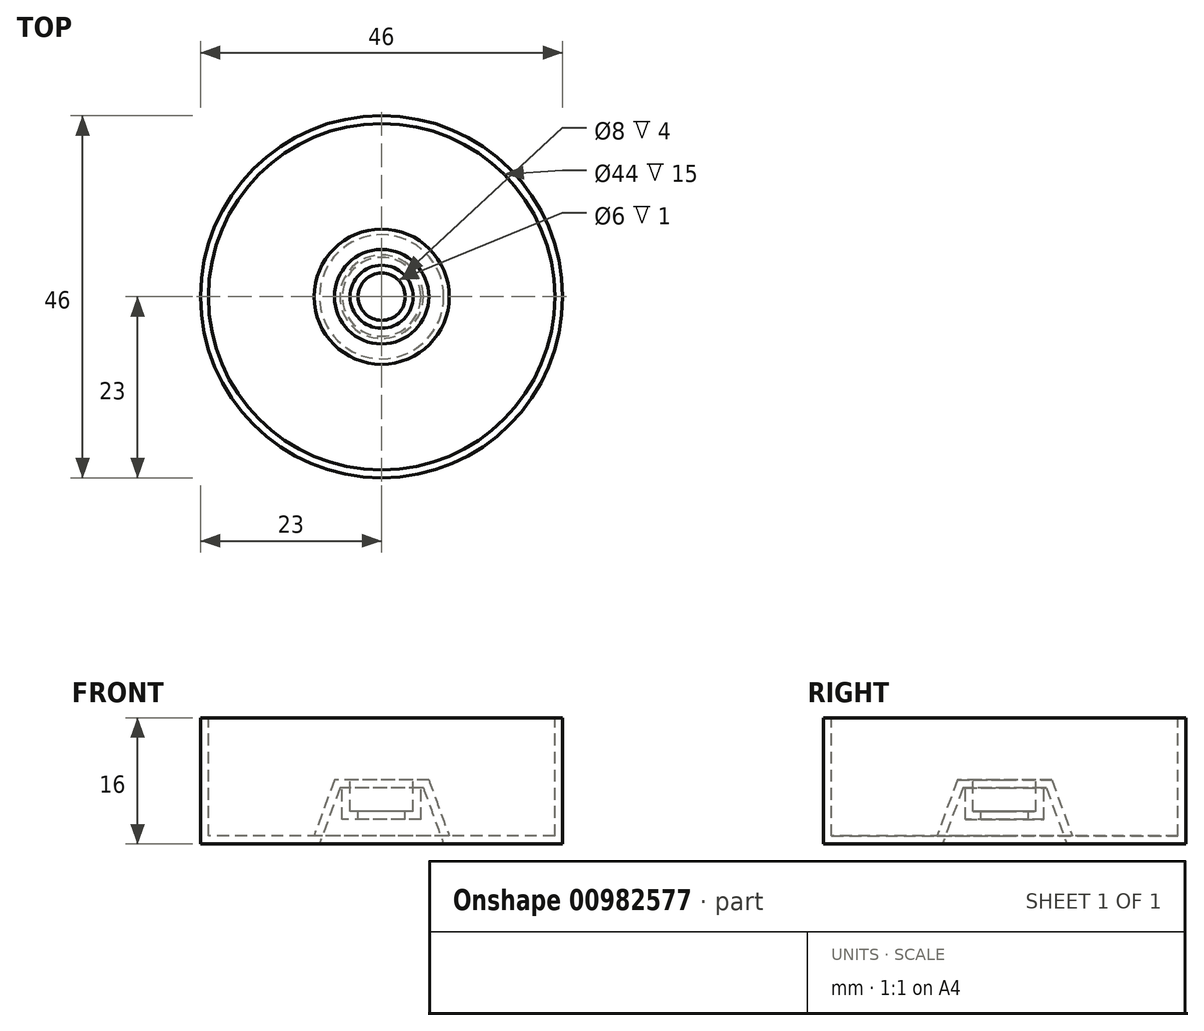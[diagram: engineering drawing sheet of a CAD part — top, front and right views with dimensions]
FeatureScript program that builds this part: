
annotation { "Feature Type Name" : "Feature", "Feature Type Description" : "" }
export const myFeature = defineFeature(function(context is Context, id is Id, definition is map)
    precondition{}
    {
        {
            var Q0;
            Q0=qCreatedBy(makeId("Front.planeOp"),FACE);
            var sketch = newSketch(context, id + "F0", { "sketchPlane" : qUnion([Q0])});
            skLineSegment(sketch, "E0", {"start": v(0, 0) * mm, "end": v(0, 17.44) * mm, "construction": true});
            skLineSegment(sketch, "E1.0", {"start": v(-4, 0) * mm, "end": v(-4, 4) * mm});
            skLineSegment(sketch, "E2", {"start": v(-3, 0) * mm, "end": v(-4, 0) * mm});
            skLineSegment(sketch, "E3", {"start": v(-4, 4) * mm, "end": v(-6, 4) * mm});
            skLineSegment(sketch, "E4", {"start": v(-7.88, -4.1) * mm, "end": v(-23, -4.1) * mm});
            skLineSegment(sketch, "E5", {"start": v(-22, -3.1) * mm, "end": v(-22, 11.9) * mm});
            skLineSegment(sketch, "E6.0", {"start": v(-3, -1) * mm, "end": v(-5, -1) * mm});
            skLineSegment(sketch, "E7.0", {"start": v(-5, -1) * mm, "end": v(-5, 3) * mm});
            skLineSegment(sketch, "E8.0", {"start": v(-5, 3) * mm, "end": v(-5.3, 3) * mm});
            skLineSegment(sketch, "E9", {"start": v(-6, 4) * mm, "end": v(-8.58, -3.1) * mm});
            skLineSegment(sketch, "E10.0", {"start": v(-5.3, 3) * mm, "end": v(-7.88, -4.1) * mm});
            skLineSegment(sketch, "E11", {"start": v(-3, 0) * mm, "end": v(-22.08, 0) * mm, "construction": true});
            skLineSegment(sketch, "E12.0", {"start": v(-8.58, -3.1) * mm, "end": v(-22, -3.1) * mm});
            skLineSegment(sketch, "E13.0", {"start": v(-23, -4.1) * mm, "end": v(-23, 11.9) * mm});
            skLineSegment(sketch, "E14.0", {"start": v(-22, 11.9) * mm, "end": v(-23, 11.9) * mm});
            skLineSegment(sketch, "E15.0", {"start": v(-3, -1) * mm, "end": v(-3, 0) * mm});
            skSolve(sketch);
        }
        {
            var Q0;
            Q0 = qConstructionFilter(qBodyType(qCreatedBy(id + "F0" ,EDGE), BodyType.WIRE), ConstructionObject.NO);
            var Q1;
            Q1=sQuery(id+"F0.wireOp",EDGE,"E0");
            revolve(context, id + "F1", {"bodyType" : ToolBodyType.SURFACE, "surfaceOperationType" : NewSurfaceOperationType.NEW, "surfaceEntities" : qUnion([Q0]), "axis" : qUnion([Q1]), "revolveType" : RevolveType.FULL});
        }
    });
